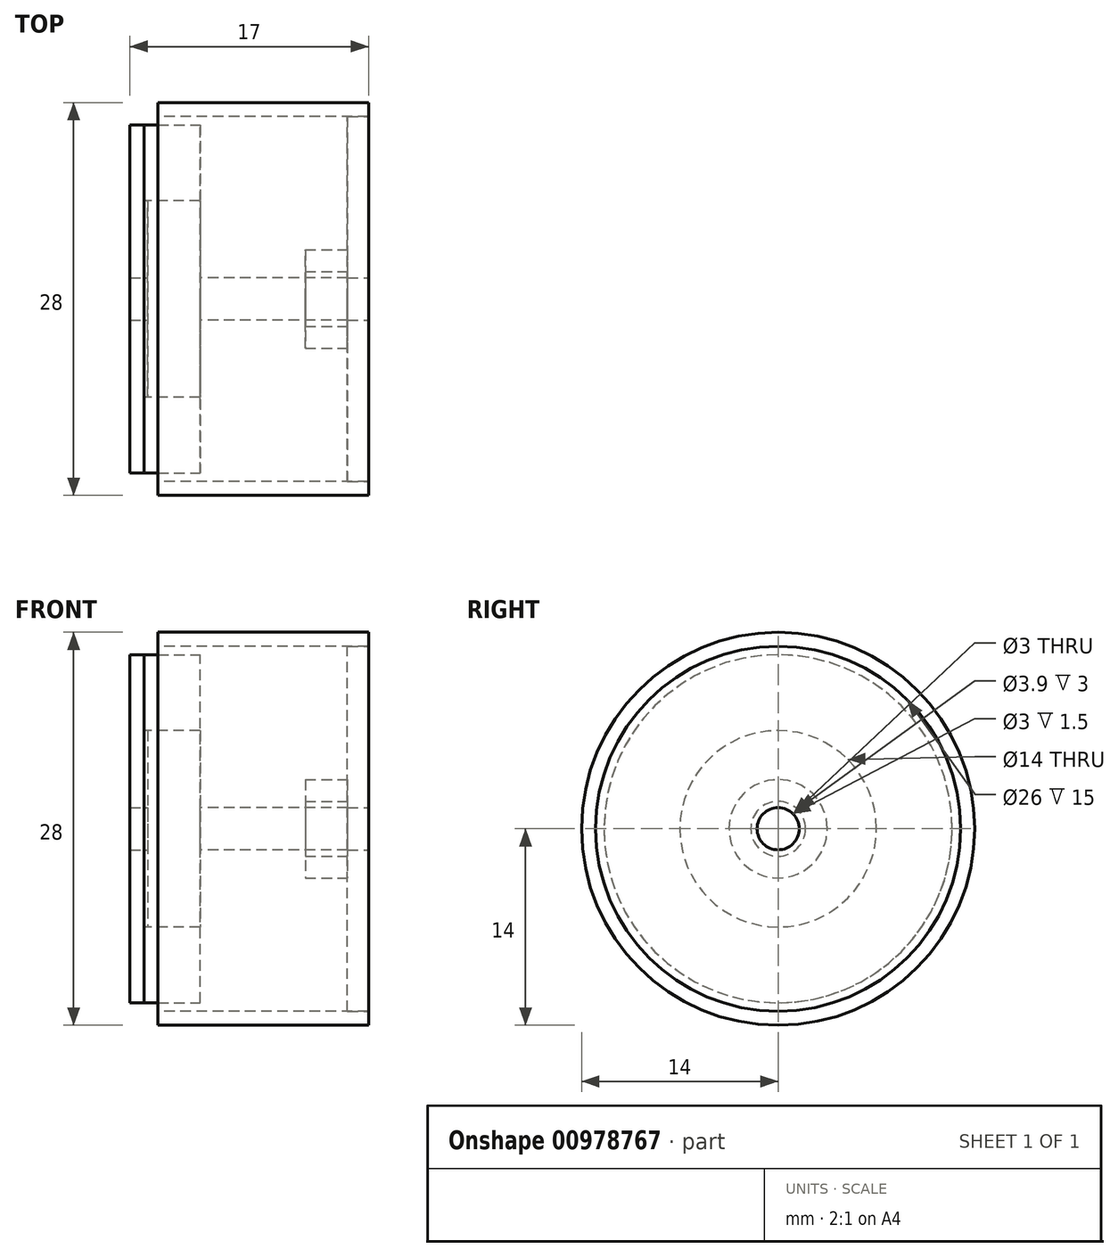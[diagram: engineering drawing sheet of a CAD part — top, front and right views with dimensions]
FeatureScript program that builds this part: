
annotation { "Feature Type Name" : "Feature", "Feature Type Description" : "" }
export const myFeature = defineFeature(function(context is Context, id is Id, definition is map)
    precondition{}
    {
        {
            var Q0;
            Q0=qCreatedBy(makeId("Right.planeOp"),FACE);
            var sketch = newSketch(context, id + "F0", { "sketchPlane" : qUnion([Q0])});
            skCircle(sketch, "E0", {"center": v(0, 0) * mm, "radius": 5.25 * mm});
            skCircle(sketch, "E1", {"center": v(0, 0) * mm, "radius": 13 * mm});
            skCircle(sketch, "E2", {"center": v(0, 0) * mm, "radius": 14 * mm});
            skCircle(sketch, "E3", {"center": v(0, 0) * mm, "radius": 1.5 * mm});
            skLineSegment(sketch, "E4", {"start": v(0, 1.5) * mm, "end": v(0, 14) * mm});
            skLineSegment(sketch, "E5", {"start": v(0, -1.5) * mm, "end": v(0, -14) * mm});
            skLineSegment(sketch, "E6", {"start": v(1.5, 0) * mm, "end": v(14, 0) * mm});
            skLineSegment(sketch, "E7", {"start": v(-1.5, 0) * mm, "end": v(-14, 0) * mm});
            skLineSegment(sketch, "E8", {"start": v(1.06, 1.06) * mm, "end": v(3.71, 3.71) * mm});
            skLineSegment(sketch, "E9", {"start": v(-1.06, 1.06) * mm, "end": v(-3.71, 3.71) * mm});
            skLineSegment(sketch, "E10", {"start": v(1.06, -1.06) * mm, "end": v(3.71, -3.71) * mm});
            skLineSegment(sketch, "E11", {"start": v(-1.06, -1.06) * mm, "end": v(-3.71, -3.71) * mm});
            skLineSegment(sketch, "E12", {"start": v(0, 5.25) * mm, "end": v(0, 13) * mm});
            skLineSegment(sketch, "E13", {"start": v(5.25, 0) * mm, "end": v(13, 0) * mm});
            skLineSegment(sketch, "E14", {"start": v(0, -5.25) * mm, "end": v(0, -13) * mm});
            skLineSegment(sketch, "E15", {"start": v(-5.25, 0) * mm, "end": v(-13, 0) * mm});
            skCircle(sketch, "E16", {"center": v(0, 9.13) * mm, "radius": 3.88 * mm});
            skCircle(sketch, "E17", {"center": v(-9.13, 0) * mm, "radius": 3.88 * mm});
            skCircle(sketch, "E18", {"center": v(9.13, 0) * mm, "radius": 3.88 * mm});
            skCircle(sketch, "E19", {"center": v(0, -9.13) * mm, "radius": 3.88 * mm});
            skLineSegment(sketch, "E20.trimOffspring", {"start": v(-9.2, 9.2) * mm, "end": v(-9.9, 9.9) * mm});
            skLineSegment(sketch, "E21.trimOffspring", {"start": v(9.2, 9.2) * mm, "end": v(9.9, 9.9) * mm});
            skLineSegment(sketch, "E22.trimOffspring", {"start": v(9.2, -9.2) * mm, "end": v(9.9, -9.9) * mm});
            skLineSegment(sketch, "E23.trimOffspring", {"start": v(-9.2, -9.2) * mm, "end": v(-9.9, -9.9) * mm});
            skSolve(sketch);
        }
        {
            var Q0;
            Q0=makeQuery(id+"F0.imprint","IMPRINT",FACE,{"disambiguationData":[TD([[makeQuery(id+"F0.imprint","IMPRINT",EDGE,{"derivedFrom":sQuery(id+"F0.wireOp",EDGE,"E1")}),-1.0]])]});
            extrude(context, id + "F1", {"entities" : qUnion([Q0]), "endBound" : BoundingType.SYMMETRIC, "depth" : 15 * mm, "offsetDistance" : 25 * mm});
        }
        {
            var Q0;
            {var subQ0=sQuery(id+"F0.wireOp",EDGE,"E3");var subQ5=makeQuery(id+"F0.imprint","INTERSECT",VERTEX,{"derivedFrom":[subQ0,sQuery(id+"F0.wireOp",EDGE,"E6")]});Q0=makeQuery(id+"F0.imprint","IMPRINT",FACE,{"disambiguationData":[TD([[makeQuery(id+"F0.imprint","IMPRINT",EDGE,{"disambiguationData":[TD([[subQ5,-1.0]])],"derivedFrom":subQ0}),1.0]])]});}
            extrude(context, id + "F2", {"entities" : qUnion([Q0]), "endBound" : BoundingType.SYMMETRIC, "depth" : 15 * mm, "offsetDistance" : 25 * mm});
        }
        {
            var Q0;
            Q0=makeQuery(id+"F2.opExtrude","CAP_FACE",FACE,{"disambiguationData":[OSD([sQuery(id+"F0.wireOp",EDGE,"E3")])],"isStart":false});
            var sketch = newSketch(context, id + "F3", { "sketchPlane" : qUnion([Q0])});
            skCircle(sketch, "E24.0", {"center": v(0, 0) * mm, "radius": 13 * mm});
            skCircle(sketch, "E25.0", {"center": v(0, 0) * mm, "radius": 1.5 * mm});
            skSolve(sketch);
        }
        {
            var Q0;
            Q0=makeQuery(id+"F3.imprint","IMPRINT",FACE,{"disambiguationData":[TD([[makeQuery(id+"F3.imprint","IMPRINT",EDGE,{"derivedFrom":sQuery(id+"F3.wireOp",EDGE,"E24.0")}),1.0]])]});
            var Q1;
            Q1=makeQuery(id+"F3.imprint","IMPRINT",FACE,{"disambiguationData":[TD([[makeQuery(id+"F3.imprint","IMPRINT",EDGE,{"derivedFrom":sQuery(id+"F3.wireOp",EDGE,"E25.0")}),1.0]])]});
            extrude(context, id + "F4", {"entities" : qUnion([Q0, Q1]), "oppositeDirection" : true, "depth" : 1.5 * mm, "offsetDistance" : 25 * mm});
        }
        {
            var Q0;
            Q0=makeQuery(id+"F4.opExtrude","CAP_FACE",FACE,{"disambiguationData":[OSD([sQuery(id+"F3.wireOp",EDGE,"E24.0")])],"isStart":false});
            var sketch = newSketch(context, id + "F5", { "sketchPlane" : qUnion([Q0])});
            skCircle(sketch, "E26.0.0", {"center": v(0, 0) * mm, "radius": 13 * mm});
            skCircle(sketch, "E27.0", {"center": v(0, 0) * mm, "radius": 1.5 * mm});
            skCircle(sketch, "E28", {"center": v(0, 0) * mm, "radius": 3.5 * mm});
            skCircle(sketch, "E29", {"center": v(0, 0) * mm, "radius": 1.95 * mm});
            skSolve(sketch);
        }
        {
            var Q0;
            Q0=makeQuery(id+"F5.imprint","IMPRINT",FACE,{"disambiguationData":[TD([[makeQuery(id+"F5.imprint","IMPRINT",EDGE,{"derivedFrom":sQuery(id+"F5.wireOp",EDGE,"E28")}),1.0]])]});
            extrude(context, id + "F6", {"entities" : qUnion([Q0]), "operationType" : NewBodyOperationType.ADD, "depth" : 3 * mm, "offsetDistance" : 25 * mm});
        }
        {
            var Q0;
            Q0=makeQuery(id+"F2.opExtrude","CAP_FACE",FACE,{"disambiguationData":[OSD([sQuery(id+"F0.wireOp",EDGE,"E3")])],"isStart":true});
            extrude(context, id + "F7", {"entities" : qUnion([Q0]), "operationType" : NewBodyOperationType.ADD, "depth" : 2 * mm, "offsetDistance" : 25 * mm});
        }
        {
            var Q0;
            Q0=makeQuery(id+"F7.opExtrude","CAP_FACE",FACE,{"disambiguationData":[OSD([sQuery(id+"F0.wireOp",EDGE,"E3")])],"isStart":false});
            var sketch = newSketch(context, id + "F8", { "sketchPlane" : qUnion([Q0])});
            skCircle(sketch, "E30.0", {"center": v(0, 0) * mm, "radius": 13 * mm});
            skSolve(sketch);
        }
        {
            var Q0;
            Q0=makeQuery(id+"F8.imprint","IMPRINT",FACE,{"disambiguationData":[TD([[makeQuery(id+"F8.imprint","IMPRINT",EDGE,{"derivedFrom":sQuery(id+"F8.wireOp",EDGE,"E30.0")}),1.0]])]});
            extrude(context, id + "F9", {"entities" : qUnion([Q0]), "oppositeDirection" : true, "depth" : 1 * mm, "offsetDistance" : 25 * mm});
        }
        {
            var Q0;
            Q0=makeQuery(id+"F7.opExtrude","CAP_FACE",FACE,{"disambiguationData":[OSD([sQuery(id+"F0.wireOp",EDGE,"E3")])],"isStart":false});
            var sketch = newSketch(context, id + "F10", { "sketchPlane" : qUnion([Q0])});
            skPoint(sketch, "E31.0", {"position": v(0, 0) * mm});
            skCircle(sketch, "E32", {"center": v(0, 0) * mm, "radius": 7 * mm});
            skSolve(sketch);
        }
        {
            var Q0;
            Q0=makeQuery(id+"F10.imprint","IMPRINT",FACE,{"disambiguationData":[TD([[makeQuery(id+"F10.imprint","IMPRINT",EDGE,{"derivedFrom":sQuery(id+"F10.wireOp",EDGE,"E32")}),1.0]])]});
            extrude(context, id + "F11", {"entities" : qUnion([Q0]), "operationType" : NewBodyOperationType.ADD, "oppositeDirection" : true, "depth" : 1.25 * mm, "offsetDistance" : 25 * mm});
        }
        {
            var Q0;
            Q0=makeQuery(id+"F2.opExtrude","CAP_FACE",FACE,{"disambiguationData":[OSD([sQuery(id+"F0.wireOp",EDGE,"E3")])],"isStart":false});
            extrude(context, id + "F12", {"entities" : qUnion([Q0]), "operationType" : NewBodyOperationType.REMOVE, "oppositeDirection" : true, "depth" : 1.5 * mm, "offsetDistance" : 25 * mm});
        }
        {
            var Q0;
            Q0=makeQuery(id+"F9.opExtrude","CAP_FACE",FACE,{"disambiguationData":[OSD([sQuery(id+"F0.wireOp",EDGE,"E3"),sQuery(id+"F8.wireOp",EDGE,"E30.0")])],"isStart":false});
            extrude(context, id + "F13", {"entities" : qUnion([Q0]), "depth" : 4 * mm, "offsetDistance" : 25 * mm});
        }
        {
            var Q0;
            Q0=makeQuery(id+"F13.opExtrude","CAP_FACE",FACE,{"disambiguationData":[OSD([sQuery(id+"F0.wireOp",EDGE,"E3"),sQuery(id+"F8.wireOp",EDGE,"E30.0")])],"isStart":false});
            var sketch = newSketch(context, id + "F14", { "sketchPlane" : qUnion([Q0])});
            skCircle(sketch, "E33.0.0", {"center": v(0, 0) * mm, "radius": 13 * mm});
            skCircle(sketch, "E34", {"center": v(0, 0) * mm, "radius": 1.5 * mm});
            skCircle(sketch, "E35", {"center": v(0, 0) * mm, "radius": 12.4 * mm});
            skSolve(sketch);
        }
        {
            var Q0;
            Q0=makeQuery(id+"F14.imprint","IMPRINT",FACE,{"disambiguationData":[TD([[makeQuery(id+"F14.imprint","IMPRINT",EDGE,{"derivedFrom":sQuery(id+"F14.wireOp",EDGE,"E34")}),1.0]])]});
            extrude(context, id + "F15", {"entities" : qUnion([Q0]), "operationType" : NewBodyOperationType.REMOVE, "oppositeDirection" : true, "depth" : 25 * mm, "offsetDistance" : 25 * mm});
        }
        {
            var Q0;
            Q0=makeQuery(id+"F14.imprint","IMPRINT",FACE,{"disambiguationData":[TD([[makeQuery(id+"F14.imprint","IMPRINT",EDGE,{"derivedFrom":sQuery(id+"F14.wireOp",EDGE,"E33.0.0")}),-1.0]])]});
            extrude(context, id + "F16", {"entities" : qUnion([Q0]), "operationType" : NewBodyOperationType.REMOVE, "oppositeDirection" : true, "depth" : 25 * mm, "offsetDistance" : 25 * mm});
        }
        {
            var Q0;
            Q0=makeQuery(id+"F13.opExtrude","CAP_FACE",FACE,{"disambiguationData":[OSD([sQuery(id+"F0.wireOp",EDGE,"E3"),sQuery(id+"F8.wireOp",EDGE,"E30.0")])],"isStart":false});
            var Q1;
            Q1=makeQuery(id+"F13.opExtrude","SWEPT_BODY",BODY,{"disambiguationData":[OSD([sQuery(id+"F0.wireOp",EDGE,"E3"),sQuery(id+"F8.wireOp",EDGE,"E30.0")])]});
            shell(context, id + "F17", {"isHollow" : true, "entities" : qUnion([Q0]), "parts" : qUnion([Q1]), "thickness" : 2 * mm});
        }
    });
